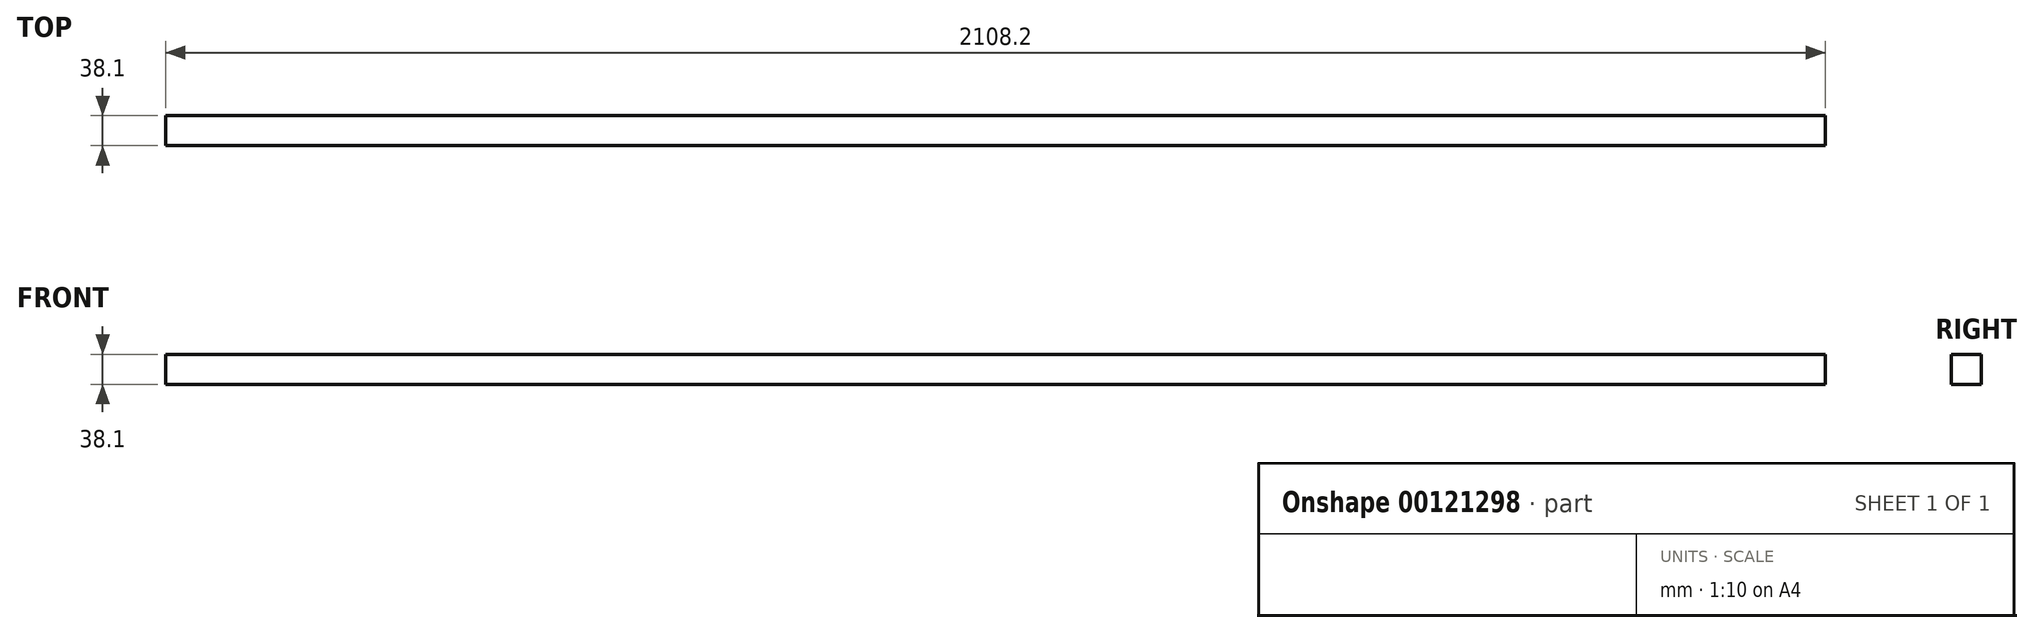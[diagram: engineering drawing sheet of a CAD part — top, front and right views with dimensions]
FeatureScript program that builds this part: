
annotation { "Feature Type Name" : "Feature", "Feature Type Description" : "" }
export const myFeature = defineFeature(function(context is Context, id is Id, definition is map)
    precondition{}
    {
        {
            var Q0;
            Q0=qCreatedBy(makeId("Front.planeOp"),FACE);
            var sketch = newSketch(context, id + "F0", { "sketchPlane" : qUnion([Q0])});
            skLineSegment(sketch, "E0.bottom", {"start": v(0, 0) * mm, "end": v(2108.2, 0) * mm});
            skLineSegment(sketch, "E0.top", {"start": v(0, 38.1) * mm, "end": v(2108.2, 38.1) * mm});
            skLineSegment(sketch, "E0.left", {"start": v(0, 0) * mm, "end": v(0, 38.1) * mm});
            skLineSegment(sketch, "E0.right", {"start": v(2108.2, 0) * mm, "end": v(2108.2, 38.1) * mm});
            skSolve(sketch);
        }
        {
            var Q0;
            Q0=makeQuery(id+"F0.imprint","IMPRINT",FACE,{"disambiguationData":[TD([[makeQuery(id+"F0.imprint","IMPRINT",EDGE,{"derivedFrom":sQuery(id+"F0.wireOp",EDGE,"E0.bottom")}),1.0]])]});
            extrude(context, id + "F1", {"entities" : qUnion([Q0]), "depth" : 38.1 * mm});
        }
    });
